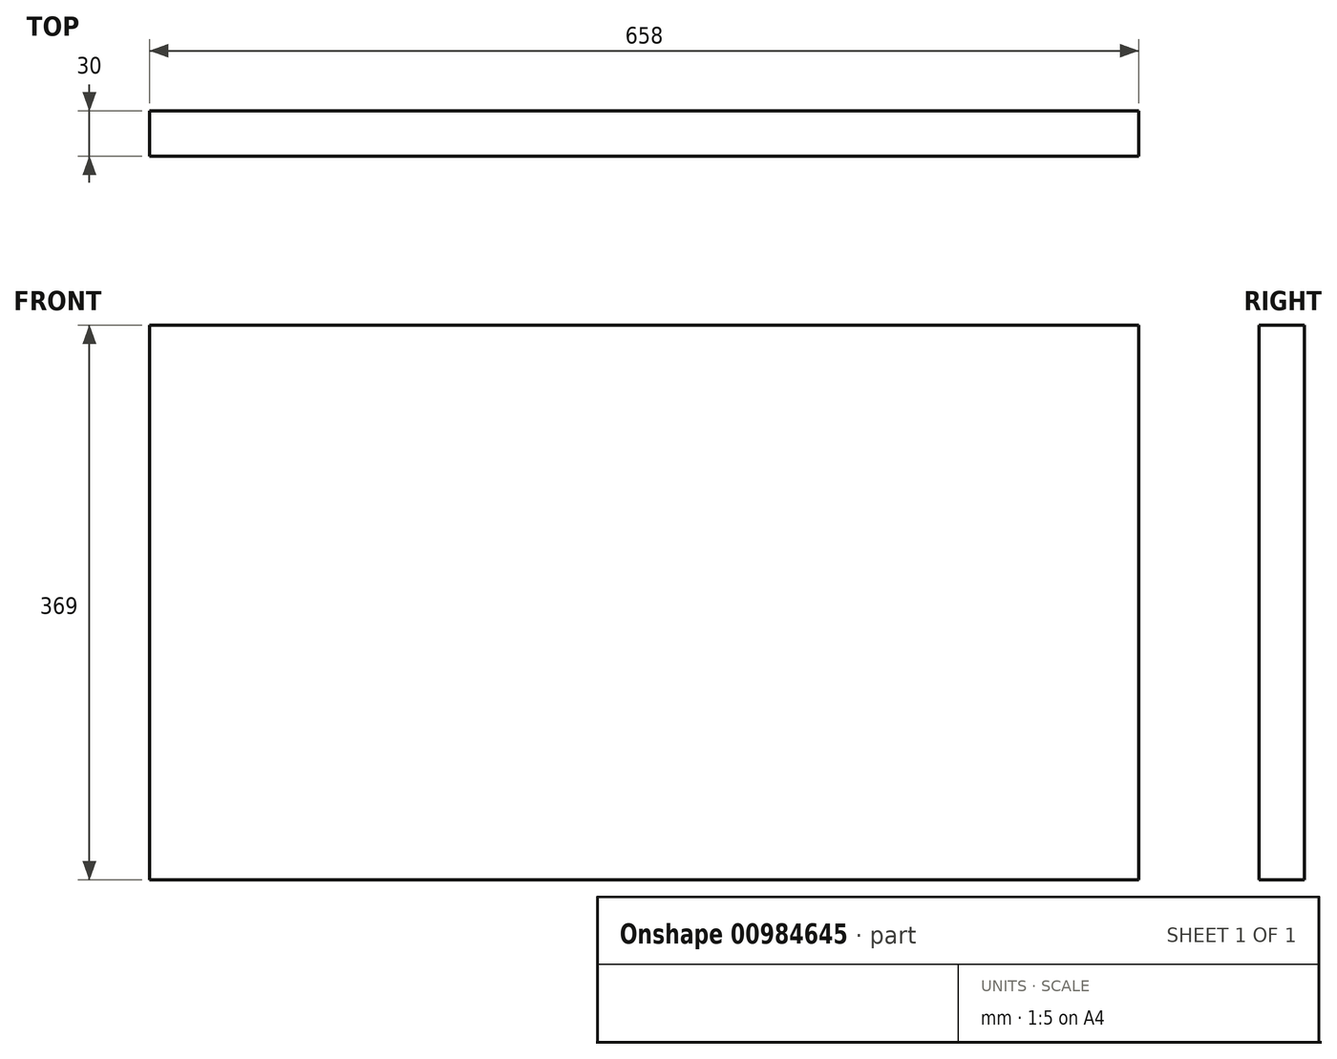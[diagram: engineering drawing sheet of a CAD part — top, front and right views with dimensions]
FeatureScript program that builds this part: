
annotation { "Feature Type Name" : "Feature", "Feature Type Description" : "" }
export const myFeature = defineFeature(function(context is Context, id is Id, definition is map)
    precondition{}
    {
        {
            var Q0;
            Q0=qCreatedBy(makeId("Front.planeOp"),FACE);
            var sketch = newSketch(context, id + "F0", { "sketchPlane" : qUnion([Q0])});
            skLineSegment(sketch, "E0.bottom", {"start": v(362.7, 140.8) * mm, "end": v(-295.3, 140.8) * mm});
            skLineSegment(sketch, "E0.top", {"start": v(362.7, -228.2) * mm, "end": v(-295.3, -228.2) * mm});
            skLineSegment(sketch, "E0.left", {"start": v(362.7, 140.8) * mm, "end": v(362.7, -228.2) * mm});
            skLineSegment(sketch, "E0.right", {"start": v(-295.3, 140.8) * mm, "end": v(-295.3, -228.2) * mm});
            skSolve(sketch);
        }
        {
            var Q0;
            Q0=makeQuery(id+"F0.imprint","IMPRINT",FACE,{"disambiguationData":[TD([[makeQuery(id+"F0.imprint","IMPRINT",EDGE,{"derivedFrom":sQuery(id+"F0.wireOp",EDGE,"E0.bottom")}),1.0]])]});
            extrude(context, id + "F1", {"entities" : qUnion([Q0]), "depth" : 30 * mm, "offsetDistance" : 25 * mm});
        }
    });
